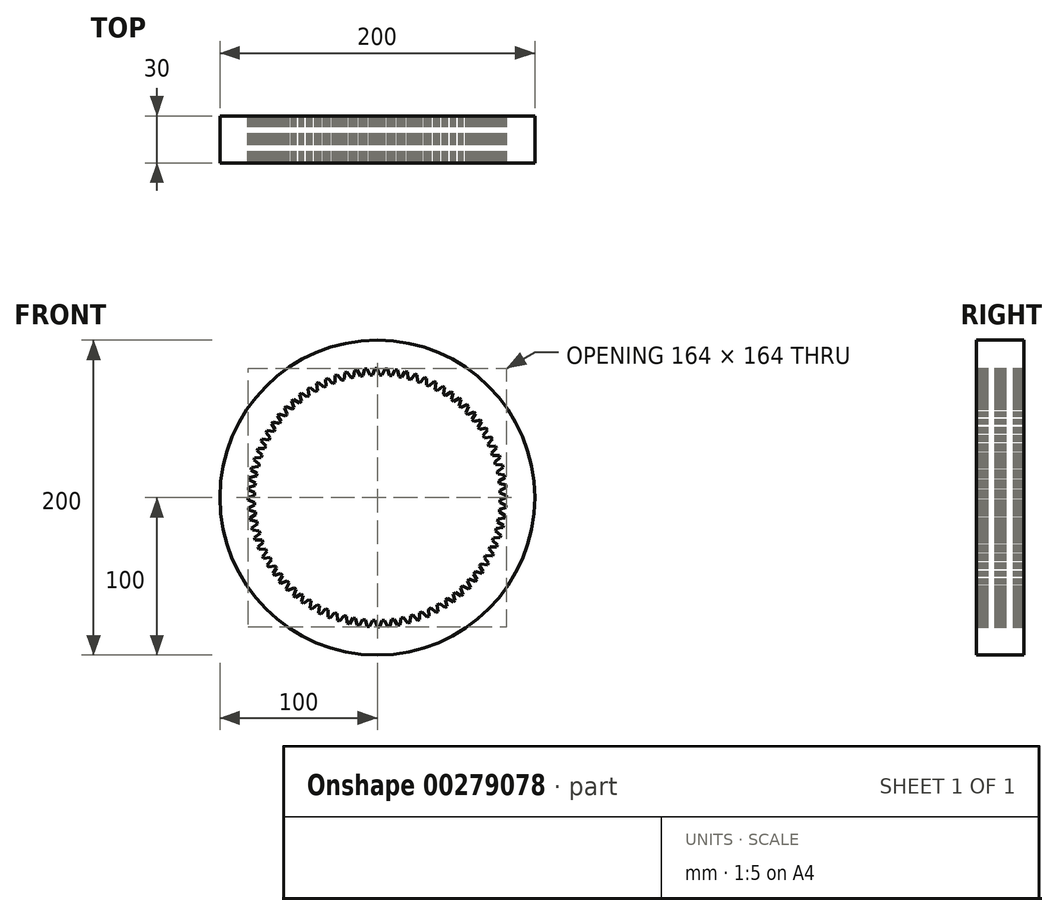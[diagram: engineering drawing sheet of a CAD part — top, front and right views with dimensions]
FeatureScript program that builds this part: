
annotation { "Feature Type Name" : "Feature", "Feature Type Description" : "" }
export const myFeature = defineFeature(function(context is Context, id is Id, definition is map)
    precondition{}
    {
        {
            var Q0;
            Q0=qCreatedBy(makeId("Front.planeOp"),FACE);
            var sketch = newSketch(context, id + "F0", { "sketchPlane" : qUnion([Q0])});
            skCircle(sketch, "E0", {"center": v(0, 0) * mm, "radius": 100 * mm});
            skPoint(sketch, "E1", {"position": v(26.3, 73.43) * mm});
            skPoint(sketch, "E2", {"position": v(27.07, 73.15) * mm});
            skPoint(sketch, "E3", {"position": v(29.96, 76.33) * mm});
            skPoint(sketch, "E4", {"position": v(31.34, 75.77) * mm});
            skPoint(sketch, "E5", {"position": v(31.22, 71.48) * mm});
            skPoint(sketch, "E6", {"position": v(31.98, 71.14) * mm});
            skLineSegment(sketch, "E7", {"start": v(26.3, 73.43) * mm, "end": v(27.07, 73.15) * mm});
            skLineSegment(sketch, "E8", {"start": v(27.07, 73.15) * mm, "end": v(29.96, 76.33) * mm});
            skLineSegment(sketch, "E9", {"start": v(29.96, 76.33) * mm, "end": v(31.34, 75.77) * mm});
            skLineSegment(sketch, "E10", {"start": v(31.34, 75.77) * mm, "end": v(31.22, 71.48) * mm});
            skLineSegment(sketch, "E11", {"start": v(31.22, 71.48) * mm, "end": v(31.98, 71.14) * mm});
            skLineSegment(sketch, "E12.1.0", {"start": v(20.45, 75.27) * mm, "end": v(21.25, 75.05) * mm});
            skLineSegment(sketch, "E12.1.1", {"start": v(21.25, 75.05) * mm, "end": v(23.88, 78.45) * mm});
            skLineSegment(sketch, "E12.1.2", {"start": v(23.88, 78.45) * mm, "end": v(25.3, 78) * mm});
            skLineSegment(sketch, "E12.1.3", {"start": v(25.3, 78) * mm, "end": v(25.51, 73.7) * mm});
            skLineSegment(sketch, "E12.1.4", {"start": v(25.51, 73.7) * mm, "end": v(26.3, 73.43) * mm});
            skLineSegment(sketch, "E12.2.0", {"start": v(14.48, 76.64) * mm, "end": v(15.3, 76.49) * mm});
            skLineSegment(sketch, "E12.2.1", {"start": v(15.3, 76.49) * mm, "end": v(17.65, 80.08) * mm});
            skLineSegment(sketch, "E12.2.2", {"start": v(17.65, 80.08) * mm, "end": v(19.1, 79.74) * mm});
            skLineSegment(sketch, "E12.2.3", {"start": v(19.1, 79.74) * mm, "end": v(19.65, 75.48) * mm});
            skLineSegment(sketch, "E12.2.4", {"start": v(19.65, 75.48) * mm, "end": v(20.45, 75.27) * mm});
            skLineSegment(sketch, "E13.1.3.0", {"start": v(8.43, 77.54) * mm, "end": v(9.25, 77.45) * mm});
            skLineSegment(sketch, "E13.3.3.0", {"start": v(9.25, 77.45) * mm, "end": v(11.32, 81.22) * mm});
            skLineSegment(sketch, "E13.6.3.0", {"start": v(11.32, 81.22) * mm, "end": v(12.78, 81) * mm});
            skLineSegment(sketch, "E13.9.3.0", {"start": v(12.78, 81) * mm, "end": v(13.67, 76.8) * mm});
            skLineSegment(sketch, "E13.12.3.0", {"start": v(13.67, 76.8) * mm, "end": v(14.48, 76.64) * mm});
            skLineSegment(sketch, "E13.1.4.0", {"start": v(2.32, 77.97) * mm, "end": v(3.14, 77.94) * mm});
            skLineSegment(sketch, "E13.3.4.0", {"start": v(3.14, 77.94) * mm, "end": v(4.9, 81.85) * mm});
            skLineSegment(sketch, "E13.6.4.0", {"start": v(4.9, 81.85) * mm, "end": v(6.39, 81.75) * mm});
            skLineSegment(sketch, "E13.9.4.0", {"start": v(6.39, 81.75) * mm, "end": v(7.6, 77.63) * mm});
            skLineSegment(sketch, "E13.12.4.0", {"start": v(7.6, 77.63) * mm, "end": v(8.43, 77.54) * mm});
            skLineSegment(sketch, "E13.1.5.0", {"start": v(-3.8, 77.9) * mm, "end": v(-2.98, 77.94) * mm});
            skLineSegment(sketch, "E13.3.5.0", {"start": v(-2.98, 77.94) * mm, "end": v(-1.53, 81.99) * mm});
            skLineSegment(sketch, "E13.6.5.0", {"start": v(-1.53, 81.99) * mm, "end": v(-0.04, 82) * mm});
            skLineSegment(sketch, "E13.9.5.0", {"start": v(-0.04, 82) * mm, "end": v(1.49, 77.99) * mm});
            skLineSegment(sketch, "E13.12.5.0", {"start": v(1.49, 77.99) * mm, "end": v(2.32, 77.97) * mm});
            skLineSegment(sketch, "E13.1.6.0", {"start": v(-9.9, 77.37) * mm, "end": v(-9.09, 77.47) * mm});
            skLineSegment(sketch, "E13.3.6.0", {"start": v(-9.09, 77.47) * mm, "end": v(-7.96, 81.61) * mm});
            skLineSegment(sketch, "E13.6.6.0", {"start": v(-7.96, 81.61) * mm, "end": v(-6.48, 81.74) * mm});
            skLineSegment(sketch, "E13.9.6.0", {"start": v(-6.48, 81.74) * mm, "end": v(-4.64, 77.86) * mm});
            skLineSegment(sketch, "E13.12.6.0", {"start": v(-4.64, 77.86) * mm, "end": v(-3.8, 77.9) * mm});
            skLineSegment(sketch, "E13.1.7.0", {"start": v(-15.95, 76.35) * mm, "end": v(-15.14, 76.52) * mm});
            skLineSegment(sketch, "E13.3.7.0", {"start": v(-15.14, 76.52) * mm, "end": v(-14.33, 80.74) * mm});
            skLineSegment(sketch, "E13.6.7.0", {"start": v(-14.33, 80.74) * mm, "end": v(-12.87, 80.98) * mm});
            skLineSegment(sketch, "E13.9.7.0", {"start": v(-12.87, 80.98) * mm, "end": v(-10.73, 77.26) * mm});
            skLineSegment(sketch, "E13.12.7.0", {"start": v(-10.73, 77.26) * mm, "end": v(-9.9, 77.37) * mm});
            skLineSegment(sketch, "E13.1.8.0", {"start": v(-21.9, 74.87) * mm, "end": v(-21.1, 75.1) * mm});
            skLineSegment(sketch, "E13.3.8.0", {"start": v(-21.1, 75.1) * mm, "end": v(-20.62, 79.36) * mm});
            skLineSegment(sketch, "E13.6.8.0", {"start": v(-20.62, 79.36) * mm, "end": v(-19.19, 79.72) * mm});
            skLineSegment(sketch, "E13.9.8.0", {"start": v(-19.19, 79.72) * mm, "end": v(-16.76, 76.18) * mm});
            skLineSegment(sketch, "E13.12.8.0", {"start": v(-16.76, 76.18) * mm, "end": v(-15.95, 76.35) * mm});
            skLineSegment(sketch, "E13.1.9.0", {"start": v(-27.7, 72.92) * mm, "end": v(-26.92, 73.2) * mm});
            skLineSegment(sketch, "E13.3.9.0", {"start": v(-26.92, 73.2) * mm, "end": v(-26.79, 77.5) * mm});
            skLineSegment(sketch, "E13.6.9.0", {"start": v(-26.79, 77.5) * mm, "end": v(-25.38, 77.97) * mm});
            skLineSegment(sketch, "E13.9.9.0", {"start": v(-25.38, 77.97) * mm, "end": v(-22.69, 74.63) * mm});
            skLineSegment(sketch, "E13.12.9.0", {"start": v(-22.69, 74.63) * mm, "end": v(-21.9, 74.87) * mm});
            skLineSegment(sketch, "E13.1.10.0", {"start": v(-33.33, 70.52) * mm, "end": v(-32.58, 70.87) * mm});
            skLineSegment(sketch, "E13.3.10.0", {"start": v(-32.58, 70.87) * mm, "end": v(-32.79, 75.16) * mm});
            skLineSegment(sketch, "E13.6.10.0", {"start": v(-32.79, 75.16) * mm, "end": v(-31.42, 75.74) * mm});
            skLineSegment(sketch, "E13.9.10.0", {"start": v(-31.42, 75.74) * mm, "end": v(-28.47, 72.62) * mm});
            skLineSegment(sketch, "E13.12.10.0", {"start": v(-28.47, 72.62) * mm, "end": v(-27.7, 72.92) * mm});
            skLineSegment(sketch, "E13.1.11.0", {"start": v(-38.76, 67.69) * mm, "end": v(-38.04, 68.1) * mm});
            skLineSegment(sketch, "E13.3.11.0", {"start": v(-38.04, 68.1) * mm, "end": v(-38.58, 72.36) * mm});
            skLineSegment(sketch, "E13.6.11.0", {"start": v(-38.58, 72.36) * mm, "end": v(-37.27, 73.04) * mm});
            skLineSegment(sketch, "E13.9.11.0", {"start": v(-37.27, 73.04) * mm, "end": v(-34.08, 70.16) * mm});
            skLineSegment(sketch, "E13.12.11.0", {"start": v(-34.08, 70.16) * mm, "end": v(-33.33, 70.52) * mm});
            skLineSegment(sketch, "E13.1.12.0", {"start": v(-43.95, 64.44) * mm, "end": v(-43.27, 64.9) * mm});
            skLineSegment(sketch, "E13.3.12.0", {"start": v(-43.27, 64.9) * mm, "end": v(-44.14, 69.1) * mm});
            skLineSegment(sketch, "E13.6.12.0", {"start": v(-44.14, 69.1) * mm, "end": v(-42.88, 69.9) * mm});
            skLineSegment(sketch, "E13.9.12.0", {"start": v(-42.88, 69.9) * mm, "end": v(-39.48, 67.27) * mm});
            skLineSegment(sketch, "E13.12.12.0", {"start": v(-39.48, 67.27) * mm, "end": v(-38.76, 67.69) * mm});
            skLineSegment(sketch, "E13.1.13.0", {"start": v(-48.87, 60.79) * mm, "end": v(-48.22, 61.3) * mm});
            skLineSegment(sketch, "E13.3.13.0", {"start": v(-48.22, 61.3) * mm, "end": v(-49.43, 65.43) * mm});
            skLineSegment(sketch, "E13.6.13.0", {"start": v(-49.43, 65.43) * mm, "end": v(-48.23, 66.31) * mm});
            skLineSegment(sketch, "E13.9.13.0", {"start": v(-48.23, 66.31) * mm, "end": v(-44.64, 63.97) * mm});
            skLineSegment(sketch, "E13.12.13.0", {"start": v(-44.64, 63.97) * mm, "end": v(-43.95, 64.44) * mm});
            skLineSegment(sketch, "E13.1.14.0", {"start": v(-53.5, 56.77) * mm, "end": v(-52.89, 57.33) * mm});
            skLineSegment(sketch, "E13.3.14.0", {"start": v(-52.89, 57.33) * mm, "end": v(-54.4, 61.35) * mm});
            skLineSegment(sketch, "E13.6.14.0", {"start": v(-54.4, 61.35) * mm, "end": v(-53.29, 62.32) * mm});
            skLineSegment(sketch, "E13.9.14.0", {"start": v(-53.29, 62.32) * mm, "end": v(-49.52, 60.27) * mm});
            skLineSegment(sketch, "E13.12.14.0", {"start": v(-49.52, 60.27) * mm, "end": v(-48.87, 60.79) * mm});
            skLineSegment(sketch, "E13.1.15.0", {"start": v(-57.78, 52.4) * mm, "end": v(-57.22, 53) * mm});
            skLineSegment(sketch, "E13.3.15.0", {"start": v(-57.22, 53) * mm, "end": v(-59.05, 56.9) * mm});
            skLineSegment(sketch, "E13.6.15.0", {"start": v(-59.05, 56.9) * mm, "end": v(-58.01, 57.95) * mm});
            skLineSegment(sketch, "E13.9.15.0", {"start": v(-58.01, 57.95) * mm, "end": v(-54.1, 56.2) * mm});
            skLineSegment(sketch, "E13.12.15.0", {"start": v(-54.1, 56.2) * mm, "end": v(-53.5, 56.77) * mm});
            skLineSegment(sketch, "E13.1.16.0", {"start": v(-61.71, 47.7) * mm, "end": v(-61.2, 48.35) * mm});
            skLineSegment(sketch, "E13.3.16.0", {"start": v(-61.2, 48.35) * mm, "end": v(-63.33, 52.08) * mm});
            skLineSegment(sketch, "E13.6.16.0", {"start": v(-63.33, 52.08) * mm, "end": v(-62.38, 53.22) * mm});
            skLineSegment(sketch, "E13.9.16.0", {"start": v(-62.38, 53.22) * mm, "end": v(-58.34, 51.78) * mm});
            skLineSegment(sketch, "E13.12.16.0", {"start": v(-58.34, 51.78) * mm, "end": v(-57.78, 52.4) * mm});
            skLineSegment(sketch, "E13.1.17.0", {"start": v(-65.27, 42.71) * mm, "end": v(-64.8, 43.4) * mm});
            skLineSegment(sketch, "E13.3.17.0", {"start": v(-64.8, 43.4) * mm, "end": v(-67.23, 46.95) * mm});
            skLineSegment(sketch, "E13.6.17.0", {"start": v(-67.23, 46.95) * mm, "end": v(-66.37, 48.16) * mm});
            skLineSegment(sketch, "E13.9.17.0", {"start": v(-66.37, 48.16) * mm, "end": v(-62.22, 47.04) * mm});
            skLineSegment(sketch, "E13.12.17.0", {"start": v(-62.22, 47.04) * mm, "end": v(-61.71, 47.7) * mm});
            skLineSegment(sketch, "E13.1.18.0", {"start": v(-68.42, 37.46) * mm, "end": v(-68.01, 38.18) * mm});
            skLineSegment(sketch, "E13.3.18.0", {"start": v(-68.01, 38.18) * mm, "end": v(-70.7, 41.54) * mm});
            skLineSegment(sketch, "E13.6.18.0", {"start": v(-70.7, 41.54) * mm, "end": v(-69.94, 42.8) * mm});
            skLineSegment(sketch, "E13.9.18.0", {"start": v(-69.94, 42.8) * mm, "end": v(-65.72, 42.01) * mm});
            skLineSegment(sketch, "E13.12.18.0", {"start": v(-65.72, 42.01) * mm, "end": v(-65.27, 42.71) * mm});
            skLineSegment(sketch, "E13.1.19.0", {"start": v(-71.14, 31.98) * mm, "end": v(-70.8, 32.73) * mm});
            skLineSegment(sketch, "E13.3.19.0", {"start": v(-70.8, 32.73) * mm, "end": v(-73.74, 35.86) * mm});
            skLineSegment(sketch, "E13.6.19.0", {"start": v(-73.74, 35.86) * mm, "end": v(-73.08, 37.19) * mm});
            skLineSegment(sketch, "E13.9.19.0", {"start": v(-73.08, 37.19) * mm, "end": v(-68.81, 36.73) * mm});
            skLineSegment(sketch, "E13.12.19.0", {"start": v(-68.81, 36.73) * mm, "end": v(-68.42, 37.46) * mm});
            skLineSegment(sketch, "E13.1.20.0", {"start": v(-73.43, 26.3) * mm, "end": v(-73.15, 27.07) * mm});
            skLineSegment(sketch, "E13.3.20.0", {"start": v(-73.15, 27.07) * mm, "end": v(-76.33, 29.96) * mm});
            skLineSegment(sketch, "E13.6.20.0", {"start": v(-76.33, 29.96) * mm, "end": v(-75.77, 31.34) * mm});
            skLineSegment(sketch, "E13.9.20.0", {"start": v(-75.77, 31.34) * mm, "end": v(-71.48, 31.22) * mm});
            skLineSegment(sketch, "E13.12.20.0", {"start": v(-71.48, 31.22) * mm, "end": v(-71.14, 31.98) * mm});
            skLineSegment(sketch, "E13.1.21.0", {"start": v(-75.27, 20.45) * mm, "end": v(-75.05, 21.25) * mm});
            skLineSegment(sketch, "E13.3.21.0", {"start": v(-75.05, 21.25) * mm, "end": v(-78.45, 23.88) * mm});
            skLineSegment(sketch, "E13.6.21.0", {"start": v(-78.45, 23.88) * mm, "end": v(-78, 25.3) * mm});
            skLineSegment(sketch, "E13.9.21.0", {"start": v(-78, 25.3) * mm, "end": v(-73.7, 25.51) * mm});
            skLineSegment(sketch, "E13.12.21.0", {"start": v(-73.7, 25.51) * mm, "end": v(-73.43, 26.3) * mm});
            skLineSegment(sketch, "E13.1.22.0", {"start": v(-76.64, 14.48) * mm, "end": v(-76.49, 15.3) * mm});
            skLineSegment(sketch, "E13.3.22.0", {"start": v(-76.49, 15.3) * mm, "end": v(-80.08, 17.65) * mm});
            skLineSegment(sketch, "E13.6.22.0", {"start": v(-80.08, 17.65) * mm, "end": v(-79.74, 19.1) * mm});
            skLineSegment(sketch, "E13.9.22.0", {"start": v(-79.74, 19.1) * mm, "end": v(-75.48, 19.65) * mm});
            skLineSegment(sketch, "E13.12.22.0", {"start": v(-75.48, 19.65) * mm, "end": v(-75.27, 20.45) * mm});
            skLineSegment(sketch, "E13.1.23.0", {"start": v(-77.54, 8.43) * mm, "end": v(-77.45, 9.25) * mm});
            skLineSegment(sketch, "E13.3.23.0", {"start": v(-77.45, 9.25) * mm, "end": v(-81.22, 11.32) * mm});
            skLineSegment(sketch, "E13.6.23.0", {"start": v(-81.22, 11.32) * mm, "end": v(-81, 12.78) * mm});
            skLineSegment(sketch, "E13.9.23.0", {"start": v(-81, 12.78) * mm, "end": v(-76.8, 13.67) * mm});
            skLineSegment(sketch, "E13.12.23.0", {"start": v(-76.8, 13.67) * mm, "end": v(-76.64, 14.48) * mm});
            skLineSegment(sketch, "E13.1.24.0", {"start": v(-77.97, 2.32) * mm, "end": v(-77.94, 3.14) * mm});
            skLineSegment(sketch, "E13.3.24.0", {"start": v(-77.94, 3.14) * mm, "end": v(-81.85, 4.9) * mm});
            skLineSegment(sketch, "E13.6.24.0", {"start": v(-81.85, 4.9) * mm, "end": v(-81.75, 6.39) * mm});
            skLineSegment(sketch, "E13.9.24.0", {"start": v(-81.75, 6.39) * mm, "end": v(-77.63, 7.6) * mm});
            skLineSegment(sketch, "E13.12.24.0", {"start": v(-77.63, 7.6) * mm, "end": v(-77.54, 8.43) * mm});
            skLineSegment(sketch, "E13.1.25.0", {"start": v(-77.9, -3.8) * mm, "end": v(-77.94, -2.98) * mm});
            skLineSegment(sketch, "E13.3.25.0", {"start": v(-77.94, -2.98) * mm, "end": v(-81.99, -1.53) * mm});
            skLineSegment(sketch, "E13.6.25.0", {"start": v(-81.99, -1.53) * mm, "end": v(-82, -0.04) * mm});
            skLineSegment(sketch, "E13.9.25.0", {"start": v(-82, -0.04) * mm, "end": v(-77.99, 1.49) * mm});
            skLineSegment(sketch, "E13.12.25.0", {"start": v(-77.99, 1.49) * mm, "end": v(-77.97, 2.32) * mm});
            skLineSegment(sketch, "E13.1.26.0", {"start": v(-77.37, -9.9) * mm, "end": v(-77.47, -9.09) * mm});
            skLineSegment(sketch, "E13.3.26.0", {"start": v(-77.47, -9.09) * mm, "end": v(-81.61, -7.96) * mm});
            skLineSegment(sketch, "E13.6.26.0", {"start": v(-81.61, -7.96) * mm, "end": v(-81.74, -6.48) * mm});
            skLineSegment(sketch, "E13.9.26.0", {"start": v(-81.74, -6.48) * mm, "end": v(-77.86, -4.64) * mm});
            skLineSegment(sketch, "E13.12.26.0", {"start": v(-77.86, -4.64) * mm, "end": v(-77.9, -3.8) * mm});
            skLineSegment(sketch, "E13.1.27.0", {"start": v(-76.35, -15.95) * mm, "end": v(-76.52, -15.14) * mm});
            skLineSegment(sketch, "E13.3.27.0", {"start": v(-76.52, -15.14) * mm, "end": v(-80.74, -14.33) * mm});
            skLineSegment(sketch, "E13.6.27.0", {"start": v(-80.74, -14.33) * mm, "end": v(-80.98, -12.87) * mm});
            skLineSegment(sketch, "E13.9.27.0", {"start": v(-80.98, -12.87) * mm, "end": v(-77.26, -10.73) * mm});
            skLineSegment(sketch, "E13.12.27.0", {"start": v(-77.26, -10.73) * mm, "end": v(-77.37, -9.9) * mm});
            skLineSegment(sketch, "E13.1.28.0", {"start": v(-74.87, -21.9) * mm, "end": v(-75.1, -21.1) * mm});
            skLineSegment(sketch, "E13.3.28.0", {"start": v(-75.1, -21.1) * mm, "end": v(-79.36, -20.62) * mm});
            skLineSegment(sketch, "E13.6.28.0", {"start": v(-79.36, -20.62) * mm, "end": v(-79.72, -19.19) * mm});
            skLineSegment(sketch, "E13.9.28.0", {"start": v(-79.72, -19.19) * mm, "end": v(-76.18, -16.76) * mm});
            skLineSegment(sketch, "E13.12.28.0", {"start": v(-76.18, -16.76) * mm, "end": v(-76.35, -15.95) * mm});
            skLineSegment(sketch, "E13.1.29.0", {"start": v(-72.92, -27.7) * mm, "end": v(-73.2, -26.92) * mm});
            skLineSegment(sketch, "E13.3.29.0", {"start": v(-73.2, -26.92) * mm, "end": v(-77.5, -26.79) * mm});
            skLineSegment(sketch, "E13.6.29.0", {"start": v(-77.5, -26.79) * mm, "end": v(-77.97, -25.38) * mm});
            skLineSegment(sketch, "E13.9.29.0", {"start": v(-77.97, -25.38) * mm, "end": v(-74.63, -22.69) * mm});
            skLineSegment(sketch, "E13.12.29.0", {"start": v(-74.63, -22.69) * mm, "end": v(-74.87, -21.9) * mm});
            skLineSegment(sketch, "E13.1.30.0", {"start": v(-70.52, -33.33) * mm, "end": v(-70.87, -32.58) * mm});
            skLineSegment(sketch, "E13.3.30.0", {"start": v(-70.87, -32.58) * mm, "end": v(-75.16, -32.79) * mm});
            skLineSegment(sketch, "E13.6.30.0", {"start": v(-75.16, -32.79) * mm, "end": v(-75.74, -31.42) * mm});
            skLineSegment(sketch, "E13.9.30.0", {"start": v(-75.74, -31.42) * mm, "end": v(-72.62, -28.47) * mm});
            skLineSegment(sketch, "E13.12.30.0", {"start": v(-72.62, -28.47) * mm, "end": v(-72.92, -27.7) * mm});
            skLineSegment(sketch, "E13.1.31.0", {"start": v(-67.69, -38.76) * mm, "end": v(-68.1, -38.04) * mm});
            skLineSegment(sketch, "E13.3.31.0", {"start": v(-68.1, -38.04) * mm, "end": v(-72.36, -38.58) * mm});
            skLineSegment(sketch, "E13.6.31.0", {"start": v(-72.36, -38.58) * mm, "end": v(-73.04, -37.27) * mm});
            skLineSegment(sketch, "E13.9.31.0", {"start": v(-73.04, -37.27) * mm, "end": v(-70.16, -34.08) * mm});
            skLineSegment(sketch, "E13.12.31.0", {"start": v(-70.16, -34.08) * mm, "end": v(-70.52, -33.33) * mm});
            skLineSegment(sketch, "E13.1.32.0", {"start": v(-64.44, -43.95) * mm, "end": v(-64.9, -43.27) * mm});
            skLineSegment(sketch, "E13.3.32.0", {"start": v(-64.9, -43.27) * mm, "end": v(-69.1, -44.14) * mm});
            skLineSegment(sketch, "E13.6.32.0", {"start": v(-69.1, -44.14) * mm, "end": v(-69.9, -42.88) * mm});
            skLineSegment(sketch, "E13.9.32.0", {"start": v(-69.9, -42.88) * mm, "end": v(-67.27, -39.48) * mm});
            skLineSegment(sketch, "E13.12.32.0", {"start": v(-67.27, -39.48) * mm, "end": v(-67.69, -38.76) * mm});
            skLineSegment(sketch, "E13.1.33.0", {"start": v(-60.79, -48.87) * mm, "end": v(-61.3, -48.22) * mm});
            skLineSegment(sketch, "E13.3.33.0", {"start": v(-61.3, -48.22) * mm, "end": v(-65.43, -49.43) * mm});
            skLineSegment(sketch, "E13.6.33.0", {"start": v(-65.43, -49.43) * mm, "end": v(-66.31, -48.23) * mm});
            skLineSegment(sketch, "E13.9.33.0", {"start": v(-66.31, -48.23) * mm, "end": v(-63.97, -44.64) * mm});
            skLineSegment(sketch, "E13.12.33.0", {"start": v(-63.97, -44.64) * mm, "end": v(-64.44, -43.95) * mm});
            skLineSegment(sketch, "E13.1.34.0", {"start": v(-56.77, -53.5) * mm, "end": v(-57.33, -52.89) * mm});
            skLineSegment(sketch, "E13.3.34.0", {"start": v(-57.33, -52.89) * mm, "end": v(-61.35, -54.4) * mm});
            skLineSegment(sketch, "E13.6.34.0", {"start": v(-61.35, -54.4) * mm, "end": v(-62.32, -53.29) * mm});
            skLineSegment(sketch, "E13.9.34.0", {"start": v(-62.32, -53.29) * mm, "end": v(-60.27, -49.52) * mm});
            skLineSegment(sketch, "E13.12.34.0", {"start": v(-60.27, -49.52) * mm, "end": v(-60.79, -48.87) * mm});
            skLineSegment(sketch, "E13.1.35.0", {"start": v(-52.4, -57.78) * mm, "end": v(-53, -57.22) * mm});
            skLineSegment(sketch, "E13.3.35.0", {"start": v(-53, -57.22) * mm, "end": v(-56.9, -59.05) * mm});
            skLineSegment(sketch, "E13.6.35.0", {"start": v(-56.9, -59.05) * mm, "end": v(-57.95, -58.01) * mm});
            skLineSegment(sketch, "E13.9.35.0", {"start": v(-57.95, -58.01) * mm, "end": v(-56.2, -54.1) * mm});
            skLineSegment(sketch, "E13.12.35.0", {"start": v(-56.2, -54.1) * mm, "end": v(-56.77, -53.5) * mm});
            skLineSegment(sketch, "E13.1.36.0", {"start": v(-47.7, -61.71) * mm, "end": v(-48.35, -61.2) * mm});
            skLineSegment(sketch, "E13.3.36.0", {"start": v(-48.35, -61.2) * mm, "end": v(-52.08, -63.33) * mm});
            skLineSegment(sketch, "E13.6.36.0", {"start": v(-52.08, -63.33) * mm, "end": v(-53.22, -62.38) * mm});
            skLineSegment(sketch, "E13.9.36.0", {"start": v(-53.22, -62.38) * mm, "end": v(-51.78, -58.34) * mm});
            skLineSegment(sketch, "E13.12.36.0", {"start": v(-51.78, -58.34) * mm, "end": v(-52.4, -57.78) * mm});
            skLineSegment(sketch, "E13.1.37.0", {"start": v(-42.71, -65.27) * mm, "end": v(-43.4, -64.8) * mm});
            skLineSegment(sketch, "E13.3.37.0", {"start": v(-43.4, -64.8) * mm, "end": v(-46.95, -67.23) * mm});
            skLineSegment(sketch, "E13.6.37.0", {"start": v(-46.95, -67.23) * mm, "end": v(-48.16, -66.37) * mm});
            skLineSegment(sketch, "E13.9.37.0", {"start": v(-48.16, -66.37) * mm, "end": v(-47.04, -62.22) * mm});
            skLineSegment(sketch, "E13.12.37.0", {"start": v(-47.04, -62.22) * mm, "end": v(-47.7, -61.71) * mm});
            skLineSegment(sketch, "E13.1.38.0", {"start": v(-37.46, -68.42) * mm, "end": v(-38.18, -68.01) * mm});
            skLineSegment(sketch, "E13.3.38.0", {"start": v(-38.18, -68.01) * mm, "end": v(-41.54, -70.7) * mm});
            skLineSegment(sketch, "E13.6.38.0", {"start": v(-41.54, -70.7) * mm, "end": v(-42.8, -69.94) * mm});
            skLineSegment(sketch, "E13.9.38.0", {"start": v(-42.8, -69.94) * mm, "end": v(-42.01, -65.72) * mm});
            skLineSegment(sketch, "E13.12.38.0", {"start": v(-42.01, -65.72) * mm, "end": v(-42.71, -65.27) * mm});
            skLineSegment(sketch, "E13.1.39.0", {"start": v(-31.98, -71.14) * mm, "end": v(-32.73, -70.8) * mm});
            skLineSegment(sketch, "E13.3.39.0", {"start": v(-32.73, -70.8) * mm, "end": v(-35.86, -73.74) * mm});
            skLineSegment(sketch, "E13.6.39.0", {"start": v(-35.86, -73.74) * mm, "end": v(-37.19, -73.08) * mm});
            skLineSegment(sketch, "E13.9.39.0", {"start": v(-37.19, -73.08) * mm, "end": v(-36.73, -68.81) * mm});
            skLineSegment(sketch, "E13.12.39.0", {"start": v(-36.73, -68.81) * mm, "end": v(-37.46, -68.42) * mm});
            skLineSegment(sketch, "E13.1.40.0", {"start": v(-26.3, -73.43) * mm, "end": v(-27.07, -73.15) * mm});
            skLineSegment(sketch, "E13.3.40.0", {"start": v(-27.07, -73.15) * mm, "end": v(-29.96, -76.33) * mm});
            skLineSegment(sketch, "E13.6.40.0", {"start": v(-29.96, -76.33) * mm, "end": v(-31.34, -75.77) * mm});
            skLineSegment(sketch, "E13.9.40.0", {"start": v(-31.34, -75.77) * mm, "end": v(-31.22, -71.48) * mm});
            skLineSegment(sketch, "E13.12.40.0", {"start": v(-31.22, -71.48) * mm, "end": v(-31.98, -71.14) * mm});
            skLineSegment(sketch, "E13.1.41.0", {"start": v(-20.45, -75.27) * mm, "end": v(-21.25, -75.05) * mm});
            skLineSegment(sketch, "E13.3.41.0", {"start": v(-21.25, -75.05) * mm, "end": v(-23.88, -78.45) * mm});
            skLineSegment(sketch, "E13.6.41.0", {"start": v(-23.88, -78.45) * mm, "end": v(-25.3, -78) * mm});
            skLineSegment(sketch, "E13.9.41.0", {"start": v(-25.3, -78) * mm, "end": v(-25.51, -73.7) * mm});
            skLineSegment(sketch, "E13.12.41.0", {"start": v(-25.51, -73.7) * mm, "end": v(-26.3, -73.43) * mm});
            skLineSegment(sketch, "E13.1.42.0", {"start": v(-14.48, -76.64) * mm, "end": v(-15.3, -76.49) * mm});
            skLineSegment(sketch, "E13.3.42.0", {"start": v(-15.3, -76.49) * mm, "end": v(-17.65, -80.08) * mm});
            skLineSegment(sketch, "E13.6.42.0", {"start": v(-17.65, -80.08) * mm, "end": v(-19.1, -79.74) * mm});
            skLineSegment(sketch, "E13.9.42.0", {"start": v(-19.1, -79.74) * mm, "end": v(-19.65, -75.48) * mm});
            skLineSegment(sketch, "E13.12.42.0", {"start": v(-19.65, -75.48) * mm, "end": v(-20.45, -75.27) * mm});
            skLineSegment(sketch, "E13.1.43.0", {"start": v(-8.43, -77.54) * mm, "end": v(-9.25, -77.45) * mm});
            skLineSegment(sketch, "E13.3.43.0", {"start": v(-9.25, -77.45) * mm, "end": v(-11.32, -81.22) * mm});
            skLineSegment(sketch, "E13.6.43.0", {"start": v(-11.32, -81.22) * mm, "end": v(-12.78, -81) * mm});
            skLineSegment(sketch, "E13.9.43.0", {"start": v(-12.78, -81) * mm, "end": v(-13.67, -76.8) * mm});
            skLineSegment(sketch, "E13.12.43.0", {"start": v(-13.67, -76.8) * mm, "end": v(-14.48, -76.64) * mm});
            skLineSegment(sketch, "E13.1.44.0", {"start": v(-2.32, -77.97) * mm, "end": v(-3.14, -77.94) * mm});
            skLineSegment(sketch, "E13.3.44.0", {"start": v(-3.14, -77.94) * mm, "end": v(-4.9, -81.85) * mm});
            skLineSegment(sketch, "E13.6.44.0", {"start": v(-4.9, -81.85) * mm, "end": v(-6.39, -81.75) * mm});
            skLineSegment(sketch, "E13.9.44.0", {"start": v(-6.39, -81.75) * mm, "end": v(-7.6, -77.63) * mm});
            skLineSegment(sketch, "E13.12.44.0", {"start": v(-7.6, -77.63) * mm, "end": v(-8.43, -77.54) * mm});
            skLineSegment(sketch, "E13.1.45.0", {"start": v(3.8, -77.9) * mm, "end": v(2.98, -77.94) * mm});
            skLineSegment(sketch, "E13.3.45.0", {"start": v(2.98, -77.94) * mm, "end": v(1.53, -81.99) * mm});
            skLineSegment(sketch, "E13.6.45.0", {"start": v(1.53, -81.99) * mm, "end": v(0.04, -82) * mm});
            skLineSegment(sketch, "E13.9.45.0", {"start": v(0.04, -82) * mm, "end": v(-1.49, -77.99) * mm});
            skLineSegment(sketch, "E13.12.45.0", {"start": v(-1.49, -77.99) * mm, "end": v(-2.32, -77.97) * mm});
            skLineSegment(sketch, "E13.1.46.0", {"start": v(9.9, -77.37) * mm, "end": v(9.09, -77.47) * mm});
            skLineSegment(sketch, "E13.3.46.0", {"start": v(9.09, -77.47) * mm, "end": v(7.96, -81.61) * mm});
            skLineSegment(sketch, "E13.6.46.0", {"start": v(7.96, -81.61) * mm, "end": v(6.48, -81.74) * mm});
            skLineSegment(sketch, "E13.9.46.0", {"start": v(6.48, -81.74) * mm, "end": v(4.64, -77.86) * mm});
            skLineSegment(sketch, "E13.12.46.0", {"start": v(4.64, -77.86) * mm, "end": v(3.8, -77.9) * mm});
            skLineSegment(sketch, "E13.1.47.0", {"start": v(15.95, -76.35) * mm, "end": v(15.14, -76.52) * mm});
            skLineSegment(sketch, "E13.3.47.0", {"start": v(15.14, -76.52) * mm, "end": v(14.33, -80.74) * mm});
            skLineSegment(sketch, "E13.6.47.0", {"start": v(14.33, -80.74) * mm, "end": v(12.87, -80.98) * mm});
            skLineSegment(sketch, "E13.9.47.0", {"start": v(12.87, -80.98) * mm, "end": v(10.73, -77.26) * mm});
            skLineSegment(sketch, "E13.12.47.0", {"start": v(10.73, -77.26) * mm, "end": v(9.9, -77.37) * mm});
            skLineSegment(sketch, "E13.1.48.0", {"start": v(21.9, -74.87) * mm, "end": v(21.1, -75.1) * mm});
            skLineSegment(sketch, "E13.3.48.0", {"start": v(21.1, -75.1) * mm, "end": v(20.62, -79.36) * mm});
            skLineSegment(sketch, "E13.6.48.0", {"start": v(20.62, -79.36) * mm, "end": v(19.19, -79.72) * mm});
            skLineSegment(sketch, "E13.9.48.0", {"start": v(19.19, -79.72) * mm, "end": v(16.76, -76.18) * mm});
            skLineSegment(sketch, "E13.12.48.0", {"start": v(16.76, -76.18) * mm, "end": v(15.95, -76.35) * mm});
            skLineSegment(sketch, "E13.1.49.0", {"start": v(27.7, -72.92) * mm, "end": v(26.92, -73.2) * mm});
            skLineSegment(sketch, "E13.3.49.0", {"start": v(26.92, -73.2) * mm, "end": v(26.79, -77.5) * mm});
            skLineSegment(sketch, "E13.6.49.0", {"start": v(26.79, -77.5) * mm, "end": v(25.38, -77.97) * mm});
            skLineSegment(sketch, "E13.9.49.0", {"start": v(25.38, -77.97) * mm, "end": v(22.69, -74.63) * mm});
            skLineSegment(sketch, "E13.12.49.0", {"start": v(22.69, -74.63) * mm, "end": v(21.9, -74.87) * mm});
            skLineSegment(sketch, "E13.1.50.0", {"start": v(33.33, -70.52) * mm, "end": v(32.58, -70.87) * mm});
            skLineSegment(sketch, "E13.3.50.0", {"start": v(32.58, -70.87) * mm, "end": v(32.79, -75.16) * mm});
            skLineSegment(sketch, "E13.6.50.0", {"start": v(32.79, -75.16) * mm, "end": v(31.42, -75.74) * mm});
            skLineSegment(sketch, "E13.9.50.0", {"start": v(31.42, -75.74) * mm, "end": v(28.47, -72.62) * mm});
            skLineSegment(sketch, "E13.12.50.0", {"start": v(28.47, -72.62) * mm, "end": v(27.7, -72.92) * mm});
            skLineSegment(sketch, "E13.1.51.0", {"start": v(38.76, -67.69) * mm, "end": v(38.04, -68.1) * mm});
            skLineSegment(sketch, "E13.3.51.0", {"start": v(38.04, -68.1) * mm, "end": v(38.58, -72.36) * mm});
            skLineSegment(sketch, "E13.6.51.0", {"start": v(38.58, -72.36) * mm, "end": v(37.27, -73.04) * mm});
            skLineSegment(sketch, "E13.9.51.0", {"start": v(37.27, -73.04) * mm, "end": v(34.08, -70.16) * mm});
            skLineSegment(sketch, "E13.12.51.0", {"start": v(34.08, -70.16) * mm, "end": v(33.33, -70.52) * mm});
            skLineSegment(sketch, "E13.1.52.0", {"start": v(43.95, -64.44) * mm, "end": v(43.27, -64.9) * mm});
            skLineSegment(sketch, "E13.3.52.0", {"start": v(43.27, -64.9) * mm, "end": v(44.14, -69.1) * mm});
            skLineSegment(sketch, "E13.6.52.0", {"start": v(44.14, -69.1) * mm, "end": v(42.88, -69.9) * mm});
            skLineSegment(sketch, "E13.9.52.0", {"start": v(42.88, -69.9) * mm, "end": v(39.48, -67.27) * mm});
            skLineSegment(sketch, "E13.12.52.0", {"start": v(39.48, -67.27) * mm, "end": v(38.76, -67.69) * mm});
            skLineSegment(sketch, "E13.1.53.0", {"start": v(48.87, -60.79) * mm, "end": v(48.22, -61.3) * mm});
            skLineSegment(sketch, "E13.3.53.0", {"start": v(48.22, -61.3) * mm, "end": v(49.43, -65.43) * mm});
            skLineSegment(sketch, "E13.6.53.0", {"start": v(49.43, -65.43) * mm, "end": v(48.23, -66.31) * mm});
            skLineSegment(sketch, "E13.9.53.0", {"start": v(48.23, -66.31) * mm, "end": v(44.64, -63.97) * mm});
            skLineSegment(sketch, "E13.12.53.0", {"start": v(44.64, -63.97) * mm, "end": v(43.95, -64.44) * mm});
            skLineSegment(sketch, "E13.1.54.0", {"start": v(53.5, -56.77) * mm, "end": v(52.89, -57.33) * mm});
            skLineSegment(sketch, "E13.3.54.0", {"start": v(52.89, -57.33) * mm, "end": v(54.4, -61.35) * mm});
            skLineSegment(sketch, "E13.6.54.0", {"start": v(54.4, -61.35) * mm, "end": v(53.29, -62.32) * mm});
            skLineSegment(sketch, "E13.9.54.0", {"start": v(53.29, -62.32) * mm, "end": v(49.52, -60.27) * mm});
            skLineSegment(sketch, "E13.12.54.0", {"start": v(49.52, -60.27) * mm, "end": v(48.87, -60.79) * mm});
            skLineSegment(sketch, "E13.1.55.0", {"start": v(57.78, -52.4) * mm, "end": v(57.22, -53) * mm});
            skLineSegment(sketch, "E13.3.55.0", {"start": v(57.22, -53) * mm, "end": v(59.05, -56.9) * mm});
            skLineSegment(sketch, "E13.6.55.0", {"start": v(59.05, -56.9) * mm, "end": v(58.01, -57.95) * mm});
            skLineSegment(sketch, "E13.9.55.0", {"start": v(58.01, -57.95) * mm, "end": v(54.1, -56.2) * mm});
            skLineSegment(sketch, "E13.12.55.0", {"start": v(54.1, -56.2) * mm, "end": v(53.5, -56.77) * mm});
            skLineSegment(sketch, "E13.1.56.0", {"start": v(61.71, -47.7) * mm, "end": v(61.2, -48.35) * mm});
            skLineSegment(sketch, "E13.3.56.0", {"start": v(61.2, -48.35) * mm, "end": v(63.33, -52.08) * mm});
            skLineSegment(sketch, "E13.6.56.0", {"start": v(63.33, -52.08) * mm, "end": v(62.38, -53.22) * mm});
            skLineSegment(sketch, "E13.9.56.0", {"start": v(62.38, -53.22) * mm, "end": v(58.34, -51.78) * mm});
            skLineSegment(sketch, "E13.12.56.0", {"start": v(58.34, -51.78) * mm, "end": v(57.78, -52.4) * mm});
            skLineSegment(sketch, "E13.1.57.0", {"start": v(65.27, -42.71) * mm, "end": v(64.8, -43.4) * mm});
            skLineSegment(sketch, "E13.3.57.0", {"start": v(64.8, -43.4) * mm, "end": v(67.23, -46.95) * mm});
            skLineSegment(sketch, "E13.6.57.0", {"start": v(67.23, -46.95) * mm, "end": v(66.37, -48.16) * mm});
            skLineSegment(sketch, "E13.9.57.0", {"start": v(66.37, -48.16) * mm, "end": v(62.22, -47.04) * mm});
            skLineSegment(sketch, "E13.12.57.0", {"start": v(62.22, -47.04) * mm, "end": v(61.71, -47.7) * mm});
            skLineSegment(sketch, "E13.1.58.0", {"start": v(68.42, -37.46) * mm, "end": v(68.01, -38.18) * mm});
            skLineSegment(sketch, "E13.3.58.0", {"start": v(68.01, -38.18) * mm, "end": v(70.7, -41.54) * mm});
            skLineSegment(sketch, "E13.6.58.0", {"start": v(70.7, -41.54) * mm, "end": v(69.94, -42.8) * mm});
            skLineSegment(sketch, "E13.9.58.0", {"start": v(69.94, -42.8) * mm, "end": v(65.72, -42.01) * mm});
            skLineSegment(sketch, "E13.12.58.0", {"start": v(65.72, -42.01) * mm, "end": v(65.27, -42.71) * mm});
            skLineSegment(sketch, "E13.1.59.0", {"start": v(71.14, -31.98) * mm, "end": v(70.8, -32.73) * mm});
            skLineSegment(sketch, "E13.3.59.0", {"start": v(70.8, -32.73) * mm, "end": v(73.74, -35.86) * mm});
            skLineSegment(sketch, "E13.6.59.0", {"start": v(73.74, -35.86) * mm, "end": v(73.08, -37.19) * mm});
            skLineSegment(sketch, "E13.9.59.0", {"start": v(73.08, -37.19) * mm, "end": v(68.81, -36.73) * mm});
            skLineSegment(sketch, "E13.12.59.0", {"start": v(68.81, -36.73) * mm, "end": v(68.42, -37.46) * mm});
            skLineSegment(sketch, "E13.1.60.0", {"start": v(73.43, -26.3) * mm, "end": v(73.15, -27.07) * mm});
            skLineSegment(sketch, "E13.3.60.0", {"start": v(73.15, -27.07) * mm, "end": v(76.33, -29.96) * mm});
            skLineSegment(sketch, "E13.6.60.0", {"start": v(76.33, -29.96) * mm, "end": v(75.77, -31.34) * mm});
            skLineSegment(sketch, "E13.9.60.0", {"start": v(75.77, -31.34) * mm, "end": v(71.48, -31.22) * mm});
            skLineSegment(sketch, "E13.12.60.0", {"start": v(71.48, -31.22) * mm, "end": v(71.14, -31.98) * mm});
            skLineSegment(sketch, "E13.1.61.0", {"start": v(75.27, -20.45) * mm, "end": v(75.05, -21.25) * mm});
            skLineSegment(sketch, "E13.3.61.0", {"start": v(75.05, -21.25) * mm, "end": v(78.45, -23.88) * mm});
            skLineSegment(sketch, "E13.6.61.0", {"start": v(78.45, -23.88) * mm, "end": v(78, -25.3) * mm});
            skLineSegment(sketch, "E13.9.61.0", {"start": v(78, -25.3) * mm, "end": v(73.7, -25.51) * mm});
            skLineSegment(sketch, "E13.12.61.0", {"start": v(73.7, -25.51) * mm, "end": v(73.43, -26.3) * mm});
            skLineSegment(sketch, "E13.1.62.0", {"start": v(76.64, -14.48) * mm, "end": v(76.49, -15.3) * mm});
            skLineSegment(sketch, "E13.3.62.0", {"start": v(76.49, -15.3) * mm, "end": v(80.08, -17.65) * mm});
            skLineSegment(sketch, "E13.6.62.0", {"start": v(80.08, -17.65) * mm, "end": v(79.74, -19.1) * mm});
            skLineSegment(sketch, "E13.9.62.0", {"start": v(79.74, -19.1) * mm, "end": v(75.48, -19.65) * mm});
            skLineSegment(sketch, "E13.12.62.0", {"start": v(75.48, -19.65) * mm, "end": v(75.27, -20.45) * mm});
            skLineSegment(sketch, "E13.1.63.0", {"start": v(77.54, -8.43) * mm, "end": v(77.45, -9.25) * mm});
            skLineSegment(sketch, "E13.3.63.0", {"start": v(77.45, -9.25) * mm, "end": v(81.22, -11.32) * mm});
            skLineSegment(sketch, "E13.6.63.0", {"start": v(81.22, -11.32) * mm, "end": v(81, -12.78) * mm});
            skLineSegment(sketch, "E13.9.63.0", {"start": v(81, -12.78) * mm, "end": v(76.8, -13.67) * mm});
            skLineSegment(sketch, "E13.12.63.0", {"start": v(76.8, -13.67) * mm, "end": v(76.64, -14.48) * mm});
            skLineSegment(sketch, "E13.1.64.0", {"start": v(77.97, -2.32) * mm, "end": v(77.94, -3.14) * mm});
            skLineSegment(sketch, "E13.3.64.0", {"start": v(77.94, -3.14) * mm, "end": v(81.85, -4.9) * mm});
            skLineSegment(sketch, "E13.6.64.0", {"start": v(81.85, -4.9) * mm, "end": v(81.75, -6.39) * mm});
            skLineSegment(sketch, "E13.9.64.0", {"start": v(81.75, -6.39) * mm, "end": v(77.63, -7.6) * mm});
            skLineSegment(sketch, "E13.12.64.0", {"start": v(77.63, -7.6) * mm, "end": v(77.54, -8.43) * mm});
            skLineSegment(sketch, "E13.1.65.0", {"start": v(77.9, 3.8) * mm, "end": v(77.94, 2.98) * mm});
            skLineSegment(sketch, "E13.3.65.0", {"start": v(77.94, 2.98) * mm, "end": v(81.99, 1.53) * mm});
            skLineSegment(sketch, "E13.6.65.0", {"start": v(81.99, 1.53) * mm, "end": v(82, 0.04) * mm});
            skLineSegment(sketch, "E13.9.65.0", {"start": v(82, 0.04) * mm, "end": v(77.99, -1.49) * mm});
            skLineSegment(sketch, "E13.12.65.0", {"start": v(77.99, -1.49) * mm, "end": v(77.97, -2.32) * mm});
            skLineSegment(sketch, "E13.1.66.0", {"start": v(77.37, 9.9) * mm, "end": v(77.47, 9.09) * mm});
            skLineSegment(sketch, "E13.3.66.0", {"start": v(77.47, 9.09) * mm, "end": v(81.61, 7.96) * mm});
            skLineSegment(sketch, "E13.6.66.0", {"start": v(81.61, 7.96) * mm, "end": v(81.74, 6.48) * mm});
            skLineSegment(sketch, "E13.9.66.0", {"start": v(81.74, 6.48) * mm, "end": v(77.86, 4.64) * mm});
            skLineSegment(sketch, "E13.12.66.0", {"start": v(77.86, 4.64) * mm, "end": v(77.9, 3.8) * mm});
            skLineSegment(sketch, "E13.1.67.0", {"start": v(76.35, 15.95) * mm, "end": v(76.52, 15.14) * mm});
            skLineSegment(sketch, "E13.3.67.0", {"start": v(76.52, 15.14) * mm, "end": v(80.74, 14.33) * mm});
            skLineSegment(sketch, "E13.6.67.0", {"start": v(80.74, 14.33) * mm, "end": v(80.98, 12.87) * mm});
            skLineSegment(sketch, "E13.9.67.0", {"start": v(80.98, 12.87) * mm, "end": v(77.26, 10.73) * mm});
            skLineSegment(sketch, "E13.12.67.0", {"start": v(77.26, 10.73) * mm, "end": v(77.37, 9.9) * mm});
            skLineSegment(sketch, "E13.1.68.0", {"start": v(74.87, 21.9) * mm, "end": v(75.1, 21.1) * mm});
            skLineSegment(sketch, "E13.3.68.0", {"start": v(75.1, 21.1) * mm, "end": v(79.36, 20.62) * mm});
            skLineSegment(sketch, "E13.6.68.0", {"start": v(79.36, 20.62) * mm, "end": v(79.72, 19.19) * mm});
            skLineSegment(sketch, "E13.9.68.0", {"start": v(79.72, 19.19) * mm, "end": v(76.18, 16.76) * mm});
            skLineSegment(sketch, "E13.12.68.0", {"start": v(76.18, 16.76) * mm, "end": v(76.35, 15.95) * mm});
            skLineSegment(sketch, "E13.1.69.0", {"start": v(72.92, 27.7) * mm, "end": v(73.2, 26.92) * mm});
            skLineSegment(sketch, "E13.3.69.0", {"start": v(73.2, 26.92) * mm, "end": v(77.5, 26.79) * mm});
            skLineSegment(sketch, "E13.6.69.0", {"start": v(77.5, 26.79) * mm, "end": v(77.97, 25.38) * mm});
            skLineSegment(sketch, "E13.9.69.0", {"start": v(77.97, 25.38) * mm, "end": v(74.63, 22.69) * mm});
            skLineSegment(sketch, "E13.12.69.0", {"start": v(74.63, 22.69) * mm, "end": v(74.87, 21.9) * mm});
            skLineSegment(sketch, "E13.1.70.0", {"start": v(70.52, 33.33) * mm, "end": v(70.87, 32.58) * mm});
            skLineSegment(sketch, "E13.3.70.0", {"start": v(70.87, 32.58) * mm, "end": v(75.16, 32.79) * mm});
            skLineSegment(sketch, "E13.6.70.0", {"start": v(75.16, 32.79) * mm, "end": v(75.74, 31.42) * mm});
            skLineSegment(sketch, "E13.9.70.0", {"start": v(75.74, 31.42) * mm, "end": v(72.62, 28.47) * mm});
            skLineSegment(sketch, "E13.12.70.0", {"start": v(72.62, 28.47) * mm, "end": v(72.92, 27.7) * mm});
            skLineSegment(sketch, "E13.1.71.0", {"start": v(67.69, 38.76) * mm, "end": v(68.1, 38.04) * mm});
            skLineSegment(sketch, "E13.3.71.0", {"start": v(68.1, 38.04) * mm, "end": v(72.36, 38.58) * mm});
            skLineSegment(sketch, "E13.6.71.0", {"start": v(72.36, 38.58) * mm, "end": v(73.04, 37.27) * mm});
            skLineSegment(sketch, "E13.9.71.0", {"start": v(73.04, 37.27) * mm, "end": v(70.16, 34.08) * mm});
            skLineSegment(sketch, "E13.12.71.0", {"start": v(70.16, 34.08) * mm, "end": v(70.52, 33.33) * mm});
            skLineSegment(sketch, "E13.1.72.0", {"start": v(64.44, 43.95) * mm, "end": v(64.9, 43.27) * mm});
            skLineSegment(sketch, "E13.3.72.0", {"start": v(64.9, 43.27) * mm, "end": v(69.1, 44.14) * mm});
            skLineSegment(sketch, "E13.6.72.0", {"start": v(69.1, 44.14) * mm, "end": v(69.9, 42.88) * mm});
            skLineSegment(sketch, "E13.9.72.0", {"start": v(69.9, 42.88) * mm, "end": v(67.27, 39.48) * mm});
            skLineSegment(sketch, "E13.12.72.0", {"start": v(67.27, 39.48) * mm, "end": v(67.69, 38.76) * mm});
            skLineSegment(sketch, "E13.1.73.0", {"start": v(60.79, 48.87) * mm, "end": v(61.3, 48.22) * mm});
            skLineSegment(sketch, "E13.3.73.0", {"start": v(61.3, 48.22) * mm, "end": v(65.43, 49.43) * mm});
            skLineSegment(sketch, "E13.6.73.0", {"start": v(65.43, 49.43) * mm, "end": v(66.31, 48.23) * mm});
            skLineSegment(sketch, "E13.9.73.0", {"start": v(66.31, 48.23) * mm, "end": v(63.97, 44.64) * mm});
            skLineSegment(sketch, "E13.12.73.0", {"start": v(63.97, 44.64) * mm, "end": v(64.44, 43.95) * mm});
            skLineSegment(sketch, "E13.1.74.0", {"start": v(56.77, 53.5) * mm, "end": v(57.33, 52.89) * mm});
            skLineSegment(sketch, "E13.3.74.0", {"start": v(57.33, 52.89) * mm, "end": v(61.35, 54.4) * mm});
            skLineSegment(sketch, "E13.6.74.0", {"start": v(61.35, 54.4) * mm, "end": v(62.32, 53.29) * mm});
            skLineSegment(sketch, "E13.9.74.0", {"start": v(62.32, 53.29) * mm, "end": v(60.27, 49.52) * mm});
            skLineSegment(sketch, "E13.12.74.0", {"start": v(60.27, 49.52) * mm, "end": v(60.79, 48.87) * mm});
            skLineSegment(sketch, "E13.1.75.0", {"start": v(52.4, 57.78) * mm, "end": v(53, 57.22) * mm});
            skLineSegment(sketch, "E13.3.75.0", {"start": v(53, 57.22) * mm, "end": v(56.9, 59.05) * mm});
            skLineSegment(sketch, "E13.6.75.0", {"start": v(56.9, 59.05) * mm, "end": v(57.95, 58.01) * mm});
            skLineSegment(sketch, "E13.9.75.0", {"start": v(57.95, 58.01) * mm, "end": v(56.2, 54.1) * mm});
            skLineSegment(sketch, "E13.12.75.0", {"start": v(56.2, 54.1) * mm, "end": v(56.77, 53.5) * mm});
            skLineSegment(sketch, "E13.1.76.0", {"start": v(47.7, 61.71) * mm, "end": v(48.35, 61.2) * mm});
            skLineSegment(sketch, "E13.3.76.0", {"start": v(48.35, 61.2) * mm, "end": v(52.08, 63.33) * mm});
            skLineSegment(sketch, "E13.6.76.0", {"start": v(52.08, 63.33) * mm, "end": v(53.22, 62.38) * mm});
            skLineSegment(sketch, "E13.9.76.0", {"start": v(53.22, 62.38) * mm, "end": v(51.78, 58.34) * mm});
            skLineSegment(sketch, "E13.12.76.0", {"start": v(51.78, 58.34) * mm, "end": v(52.4, 57.78) * mm});
            skLineSegment(sketch, "E13.1.77.0", {"start": v(42.71, 65.27) * mm, "end": v(43.4, 64.8) * mm});
            skLineSegment(sketch, "E13.3.77.0", {"start": v(43.4, 64.8) * mm, "end": v(46.95, 67.23) * mm});
            skLineSegment(sketch, "E13.6.77.0", {"start": v(46.95, 67.23) * mm, "end": v(48.16, 66.37) * mm});
            skLineSegment(sketch, "E13.9.77.0", {"start": v(48.16, 66.37) * mm, "end": v(47.04, 62.22) * mm});
            skLineSegment(sketch, "E13.12.77.0", {"start": v(47.04, 62.22) * mm, "end": v(47.7, 61.71) * mm});
            skLineSegment(sketch, "E13.1.78.0", {"start": v(37.46, 68.42) * mm, "end": v(38.18, 68.01) * mm});
            skLineSegment(sketch, "E13.3.78.0", {"start": v(38.18, 68.01) * mm, "end": v(41.54, 70.7) * mm});
            skLineSegment(sketch, "E13.6.78.0", {"start": v(41.54, 70.7) * mm, "end": v(42.8, 69.94) * mm});
            skLineSegment(sketch, "E13.9.78.0", {"start": v(42.8, 69.94) * mm, "end": v(42.01, 65.72) * mm});
            skLineSegment(sketch, "E13.12.78.0", {"start": v(42.01, 65.72) * mm, "end": v(42.71, 65.27) * mm});
            skLineSegment(sketch, "E13.1.79.0", {"start": v(31.98, 71.14) * mm, "end": v(32.73, 70.8) * mm});
            skLineSegment(sketch, "E13.3.79.0", {"start": v(32.73, 70.8) * mm, "end": v(35.86, 73.74) * mm});
            skLineSegment(sketch, "E13.6.79.0", {"start": v(35.86, 73.74) * mm, "end": v(37.19, 73.08) * mm});
            skLineSegment(sketch, "E13.9.79.0", {"start": v(37.19, 73.08) * mm, "end": v(36.73, 68.81) * mm});
            skLineSegment(sketch, "E13.12.79.0", {"start": v(36.73, 68.81) * mm, "end": v(37.46, 68.42) * mm});
            skPoint(sketch, "E14.trimOffspring.end.orphan", {"position": v(92.86, 217.97) * mm});
            skPoint(sketch, "E15.trimOffspring.end.orphan", {"position": v(97.96, 217.97) * mm});
            skSolve(sketch);
        }
        {
            var Q0;
            Q0 = qSketchRegion(id + "F0", true);
            extrude(context, id + "F1", {"entities" : qUnion([Q0]), "endBound" : BoundingType.SYMMETRIC, "depth" : 30 * mm});
        }
    });
